# Revit family: Benches-Bernhardt_Design-cp.2
name_source: partatom
category: Furniture
revit_build: Autodesk Revit Architecture 2013 (Build: 20130531_2115(x64)
units: mm (PartAtom-declared; Revit-internal decimal feet)

## types (4) — shared parameters
Depth = 1' - 10"
Manufacturer = Bernhardt Design
Product Documentation Link = http://bernhardtdesign.com
Product Name = cp.1
Product Page URL = http://bernhardtdesign.com
URL = http://bernhardtdesign.com
Upholstery = Fabric - Bernhardt Design - Leather - Brown

## per-type parameters (varying)
| type | Cushion Type | Description | Height | Metal Finish | Seat Height | Width |
| 6504 | cp.2-cushion-ottoman | Ottoman | 1' - 3 7/8" | Metal - Bernhardt Design - Polished Stainless Steel | 1' - 3 7/8" | 2' - 2 3/4" |
| 6504B | cp.2-cushion-ottoman | Ottoman | 1' - 3 7/8" | Metal - Bernhardt Design - Brushed Stainless Steel | 1' - 3 7/8" | 2' - 2 3/4" |
| 6506 | cp.2-cushion-bench | Bench | 1' - 4 3/8" | Metal - Bernhardt Design - Polished Stainless Steel | 1' - 4 3/8" | 4' - 8 1/2" |
| 6506B | cp.2-cushion-bench | Bench | 1' - 4 3/8" | Metal - Bernhardt Design - Brushed Stainless Steel | 1' - 4 3/8" | 4' - 8 1/2" |

note: column(s) folded — value = type name in every type: Model

## geometry (parser evidence)
native form markers: Blend x43, Sweep x3
no freeform markers — native parametric forms only
